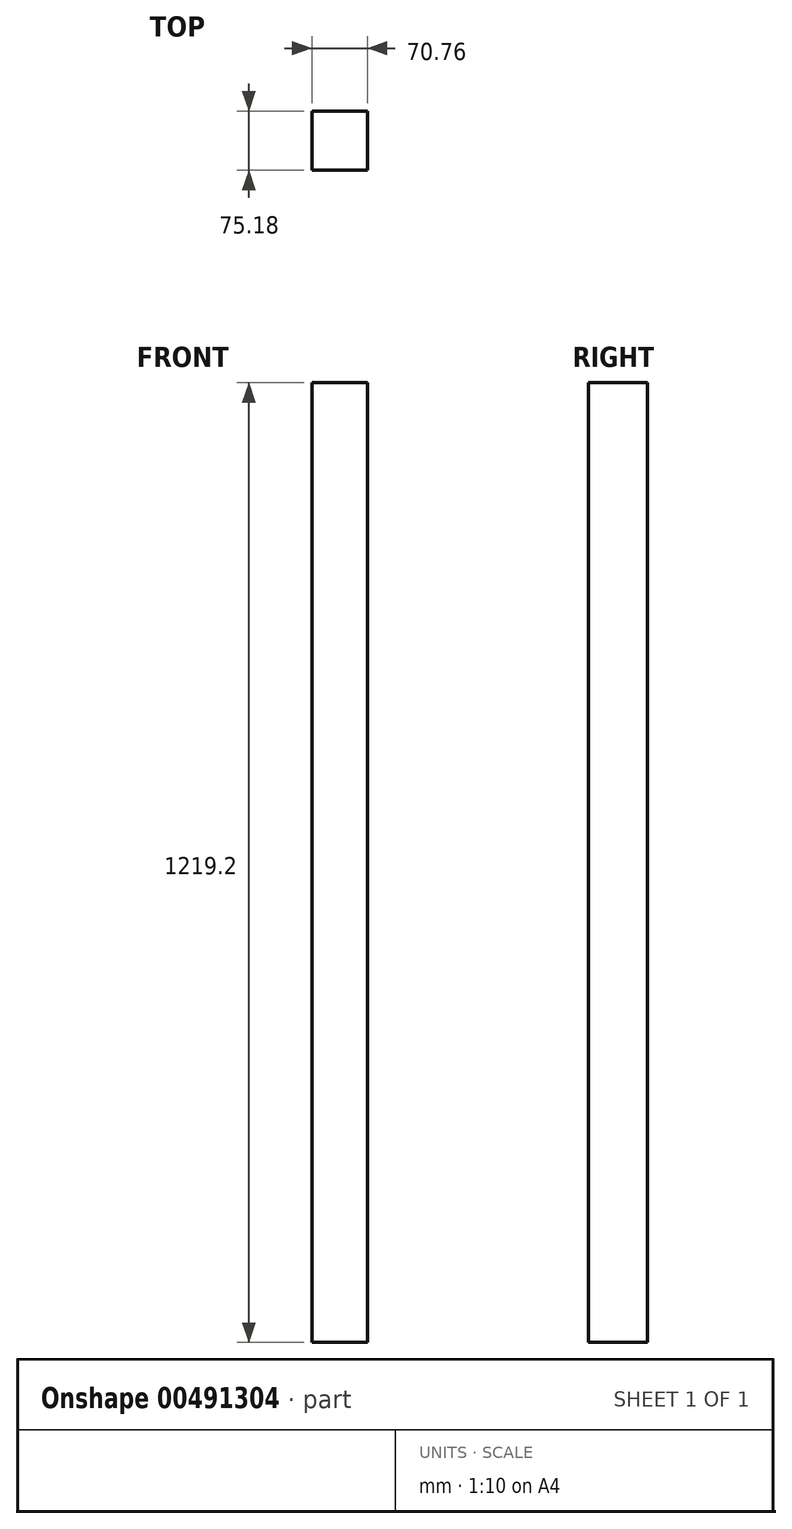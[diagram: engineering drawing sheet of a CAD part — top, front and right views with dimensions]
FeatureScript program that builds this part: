
annotation { "Feature Type Name" : "Feature", "Feature Type Description" : "" }
export const myFeature = defineFeature(function(context is Context, id is Id, definition is map)
    precondition{}
    {
        {
            var Q0;
            Q0=qCreatedBy(makeId("Top.planeOp"),FACE);
            var sketch = newSketch(context, id + "F0", { "sketchPlane" : qUnion([Q0])});
            skLineSegment(sketch, "E0.bottom", {"start": v(35.38, 37.59) * mm, "end": v(-35.38, 37.59) * mm});
            skLineSegment(sketch, "E0.top", {"start": v(35.38, -37.59) * mm, "end": v(-35.38, -37.59) * mm});
            skLineSegment(sketch, "E0.left", {"start": v(35.38, 37.59) * mm, "end": v(35.38, -37.59) * mm});
            skLineSegment(sketch, "E0.right", {"start": v(-35.38, 37.59) * mm, "end": v(-35.38, -37.59) * mm});
            skPoint(sketch, "E0.middle", {"position": v(0, 0) * mm});
            skSolve(sketch);
        }
        {
            var Q0;
            Q0 = qSketchRegion(id + "F0", true);
            extrude(context, id + "F1", {"entities" : qUnion([Q0]), "depth" : 1219.2 * mm});
        }
    });
